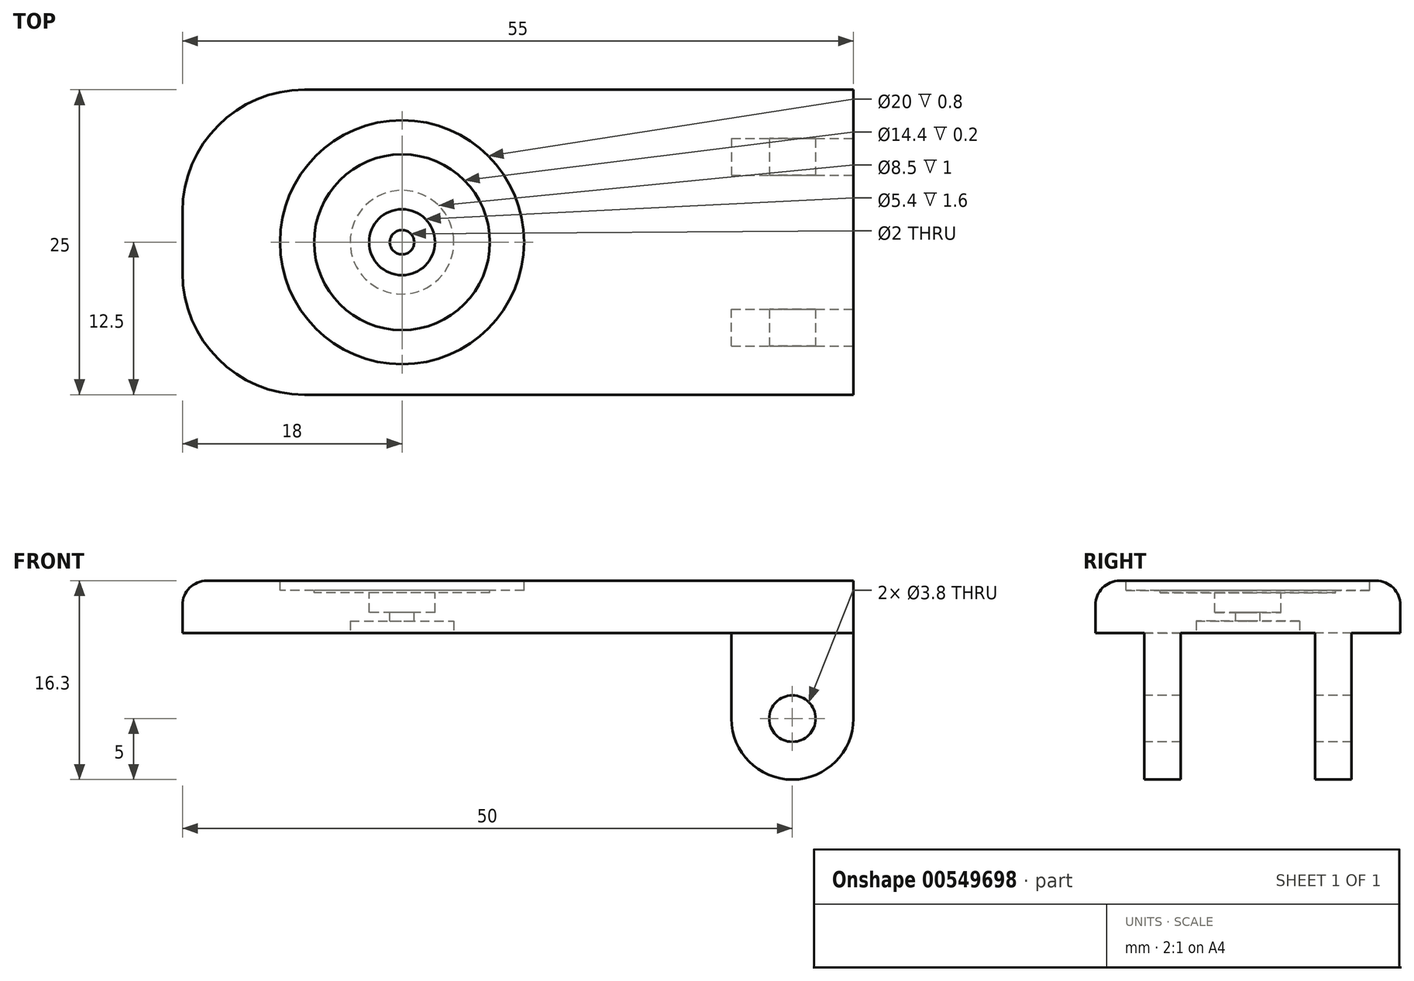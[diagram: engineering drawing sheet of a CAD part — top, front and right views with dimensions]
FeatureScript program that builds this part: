
annotation { "Feature Type Name" : "Feature", "Feature Type Description" : "" }
export const myFeature = defineFeature(function(context is Context, id is Id, definition is map)
    precondition{}
    {
        {
            var Q0;
            Q0=qCreatedBy(makeId("Top.planeOp"),FACE);
            var sketch = newSketch(context, id + "F0", { "sketchPlane" : qUnion([Q0])});
            skLineSegment(sketch, "E0.bottom", {"start": v(-45, 12.5) * mm, "end": v(0, 12.5) * mm});
            skLineSegment(sketch, "E0.top", {"start": v(-45, -12.5) * mm, "end": v(0, -12.5) * mm});
            skLineSegment(sketch, "E0.left", {"start": v(-55, 2.5) * mm, "end": v(-55, -2.5) * mm});
            skLineSegment(sketch, "E0.right", {"start": v(0, 12.5) * mm, "end": v(0, -12.5) * mm});
            skCircle(sketch, "E1", {"center": v(-37, 0) * mm, "radius": 10 * mm});
            skLineSegment(sketch, "E2", {"start": v(-55, 0) * mm, "end": v(0, 0) * mm, "construction": true});
            skPoint(sketch, "E3.visualSharp", {"position": v(-55, 12.5) * mm});
            skArc(sketch, "E3.filletArc", {"start": v(-45, 12.5) * mm, "mid": v(-52.07, 9.57) * mm, "end": v(-55, 2.5) * mm});
            skPoint(sketch, "E4.visualSharp", {"position": v(-55, -12.5) * mm});
            skArc(sketch, "E4.filletArc", {"start": v(-55, -2.5) * mm, "mid": v(-52.07, -9.57) * mm, "end": v(-45, -12.5) * mm});
            skCircle(sketch, "E5", {"center": v(-37, 0) * mm, "radius": 7.2 * mm});
            skCircle(sketch, "E6", {"center": v(-37, 0) * mm, "radius": 2.7 * mm});
            skSolve(sketch);
        }
        {
            var Q0;
            Q0 = qSketchRegion(id + "F0", true);
            var Q1;
            Q1=makeQuery(id+"F0.imprint","IMPRINT",FACE,{"disambiguationData":[TD([[makeQuery(id+"F0.imprint","IMPRINT",EDGE,{"derivedFrom":sQuery(id+"F0.wireOp",EDGE,"E1")}),1.0]])]});
            var Q2;
            Q2=makeQuery(id+"F0.imprint","IMPRINT",FACE,{"disambiguationData":[TD([[makeQuery(id+"F0.imprint","IMPRINT",EDGE,{"derivedFrom":sQuery(id+"F0.wireOp",EDGE,"E5")}),1.0]])]});
            var Q3;
            Q3=makeQuery(id+"F0.imprint","IMPRINT",FACE,{"disambiguationData":[TD([[makeQuery(id+"F0.imprint","IMPRINT",EDGE,{"derivedFrom":sQuery(id+"F0.wireOp",EDGE,"E6")}),1.0]])]});
            extrude(context, id + "F1", {"entities" : qUnion([Q0, Q1, Q2, Q3]), "oppositeDirection" : true, "depth" : 4.3 * mm, "offsetDistance" : 25 * mm});
        }
        {
            var Q0;
            Q0=makeQuery(id+"F0.imprint","IMPRINT",FACE,{"disambiguationData":[TD([[makeQuery(id+"F0.imprint","IMPRINT",EDGE,{"derivedFrom":sQuery(id+"F0.wireOp",EDGE,"E1")}),1.0]])]});
            var Q1;
            Q1=makeQuery(id+"F0.imprint","IMPRINT",FACE,{"disambiguationData":[TD([[makeQuery(id+"F0.imprint","IMPRINT",EDGE,{"derivedFrom":sQuery(id+"F0.wireOp",EDGE,"E5")}),1.0]])]});
            extrude(context, id + "F2", {"entities" : qUnion([Q0, Q1]), "operationType" : NewBodyOperationType.REMOVE, "oppositeDirection" : true, "depth" : .8 * mm, "offsetDistance" : 25 * mm});
        }
        {
            var Q0;
            Q0=makeQuery(id+"F0.imprint","IMPRINT",FACE,{"disambiguationData":[TD([[makeQuery(id+"F0.imprint","IMPRINT",EDGE,{"derivedFrom":sQuery(id+"F0.wireOp",EDGE,"E5")}),1.0]])]});
            extrude(context, id + "F3", {"entities" : qUnion([Q0]), "operationType" : NewBodyOperationType.REMOVE, "oppositeDirection" : true, "depth" : 1 * mm, "offsetDistance" : 25 * mm});
        }
        {
            var Q0;
            Q0=makeQuery(id+"F1.opExtrude","CAP_FACE",FACE,{"disambiguationData":[OSD([sQuery(id+"F0.wireOp",EDGE,"E0.bottom"),sQuery(id+"F0.wireOp",EDGE,"E0.top"),sQuery(id+"F0.wireOp",EDGE,"E0.left"),sQuery(id+"F0.wireOp",EDGE,"E0.right"),sQuery(id+"F0.wireOp",EDGE,"E3.filletArc"),sQuery(id+"F0.wireOp",EDGE,"E4.filletArc"),sQuery(id+"F0.wireOp",EDGE,"E6")])],"isStart":false});
            var sketch = newSketch(context, id + "F4", { "sketchPlane" : qUnion([Q0])});
            skCircle(sketch, "E7", {"center": v(-37, 0) * mm, "radius": 4.25 * mm});
            skLineSegment(sketch, "E8.bottom", {"start": v(-10, 8.5) * mm, "end": v(0, 8.5) * mm});
            skLineSegment(sketch, "E8.top", {"start": v(-10, 5.5) * mm, "end": v(0, 5.5) * mm});
            skLineSegment(sketch, "E8.left", {"start": v(-10, 8.5) * mm, "end": v(-10, 5.5) * mm});
            skLineSegment(sketch, "E8.right", {"start": v(0, 8.5) * mm, "end": v(0, 5.5) * mm});
            skLineSegment(sketch, "E9.MirrorCS", {"start": v(-10, -8.5) * mm, "end": v(0, -8.5) * mm});
            skLineSegment(sketch, "E10.MirrorCS", {"start": v(0, -8.5) * mm, "end": v(0, -5.5) * mm});
            skLineSegment(sketch, "E11.MirrorCS", {"start": v(-10, -5.5) * mm, "end": v(0, -5.5) * mm});
            skLineSegment(sketch, "E12.MirrorCS", {"start": v(-10, -8.5) * mm, "end": v(-10, -5.5) * mm});
            skSolve(sketch);
        }
        {
            var Q0;
            Q0=makeQuery(id+"F4.imprint","IMPRINT",FACE,{"disambiguationData":[TD([[makeQuery(id+"F4.imprint","IMPRINT",EDGE,{"derivedFrom":sQuery(id+"F4.wireOp",EDGE,"E7")}),1.0]])]});
            extrude(context, id + "F5", {"entities" : qUnion([Q0]), "operationType" : NewBodyOperationType.REMOVE, "oppositeDirection" : true, "depth" : 1 * mm, "offsetDistance" : 25 * mm});
        }
        {
            var Q0;
            Q0=makeQuery(id+"F4.imprint","IMPRINT",FACE,{"disambiguationData":[TD([[makeQuery(id+"F4.imprint","IMPRINT",EDGE,{"derivedFrom":sQuery(id+"F4.wireOp",EDGE,"E8.bottom")}),-1.0]])]});
            var Q1;
            Q1=makeQuery(id+"F4.imprint","IMPRINT",FACE,{"disambiguationData":[TD([[makeQuery(id+"F4.imprint","IMPRINT",EDGE,{"derivedFrom":sQuery(id+"F4.wireOp",EDGE,"E9.MirrorCS")}),1.0]])]});
            extrude(context, id + "F6", {"entities" : qUnion([Q0, Q1]), "operationType" : NewBodyOperationType.ADD, "depth" : 12 * mm, "offsetDistance" : 25 * mm});
        }
        {
            var Q0;
            Q0=makeQuery(id+"F6.opExtrude","SWEPT_FACE",FACE,{"disambiguationData":[OSD([sQuery(id+"F4.wireOp",EDGE,"E8.bottom")])]});
            var sketch = newSketch(context, id + "F7", { "sketchPlane" : qUnion([Q0])});
            skLineSegment(sketch, "E13", {"start": v(-5, -16.3) * mm, "end": v(-5, -4.3) * mm, "construction": true});
            skCircle(sketch, "E14", {"center": v(-5, -11.3) * mm, "radius": 1.9 * mm});
            skSolve(sketch);
        }
        {
            var Q0;
            Q0=makeQuery(id+"F6.opExtrude","CAP_EDGE",EDGE,{"disambiguationData":[OSD([sQuery(id+"F4.wireOp",EDGE,"E8.right")])],"isStart":false});
            var Q1;
            Q1=makeQuery(id+"F6.opExtrude","CAP_EDGE",EDGE,{"disambiguationData":[OSD([sQuery(id+"F4.wireOp",EDGE,"E10.MirrorCS")])],"isStart":false});
            var Q2;
            Q2=makeQuery(id+"F6.opExtrude","CAP_EDGE",EDGE,{"disambiguationData":[OSD([sQuery(id+"F4.wireOp",EDGE,"E12.MirrorCS")])],"isStart":false});
            var Q3;
            Q3=makeQuery(id+"F6.opExtrude","CAP_EDGE",EDGE,{"disambiguationData":[OSD([sQuery(id+"F4.wireOp",EDGE,"E8.left")])],"isStart":false});
            fillet(context, id + "F8", {"entities" : qUnion([Q0, Q1, Q2, Q3]), "radius" : 5 * mm, "tangentPropagation" : true, "allowEdgeOverflow" : false});
        }
        {
            var Q0;
            Q0=makeQuery(id+"F7.imprint","IMPRINT",FACE,{"disambiguationData":[TD([[makeQuery(id+"F7.imprint","IMPRINT",EDGE,{"derivedFrom":sQuery(id+"F7.wireOp",EDGE,"E14")}),1.0]])]});
            var Q1;
            Q1=sQuery(id+"F7.wireOp",EDGE,"E14");
            extrude(context, id + "F9", {"entities" : qUnion([Q0]), "operationType" : NewBodyOperationType.REMOVE, "surfaceEntities" : qUnion([Q1]), "oppositeDirection" : true, "depth" : 25 * mm, "offsetDistance" : 25 * mm});
        }
        {
            var Q0;
            Q0=makeQuery(id+"F1.opExtrude","CAP_EDGE",EDGE,{"disambiguationData":[OSD([sQuery(id+"F0.wireOp",EDGE,"E0.top")])],"isStart":true});
            fillet(context, id + "F10", {"entities" : qUnion([Q0]), "radius" : 2 * mm, "tangentPropagation" : true, "allowEdgeOverflow" : false});
        }
        {
            var Q0;
            Q0=makeQuery(id+"F2.boolean.opBoolean","SPLIT",FACE,{"disambiguationData":[TD([makeQuery(id+"F2.opExtrude","SWEPT_FACE",FACE,{"disambiguationData":[OSD([sQuery(id+"F0.wireOp",EDGE,"E6")])]})])],"derivedFrom":makeQuery(id+"F1.opExtrude","CAP_FACE",FACE,{"disambiguationData":[OSD([sQuery(id+"F0.wireOp",EDGE,"E0.bottom"),sQuery(id+"F0.wireOp",EDGE,"E0.top"),sQuery(id+"F0.wireOp",EDGE,"E0.left"),sQuery(id+"F0.wireOp",EDGE,"E0.right"),sQuery(id+"F0.wireOp",EDGE,"E3.filletArc"),sQuery(id+"F0.wireOp",EDGE,"E4.filletArc")])],"isStart":true})});
            extrude(context, id + "F11", {"entities" : qUnion([Q0]), "operationType" : NewBodyOperationType.REMOVE, "oppositeDirection" : true, "depth" : 2.6 * mm, "offsetDistance" : 25 * mm});
        }
        {
            var Q0;
            Q0=sQuery(id+"F0.wireOp",VERTEX,"E1.center");
            var Q1;
            Q1=makeQuery(id+"F1.opExtrude","SWEPT_BODY",BODY,{"disambiguationData":[OSD([sQuery(id+"F0.wireOp",EDGE,"E0.bottom"),sQuery(id+"F0.wireOp",EDGE,"E0.top"),sQuery(id+"F0.wireOp",EDGE,"E0.left"),sQuery(id+"F0.wireOp",EDGE,"E0.right"),sQuery(id+"F0.wireOp",EDGE,"E3.filletArc"),sQuery(id+"F0.wireOp",EDGE,"E4.filletArc")])]});
            hole(context, id + "F12", {"style" : HoleStyle.SIMPLE, "endStyle" : HoleEndStyle.THROUGH, "holeDiameter" : 2 * mm, "isTappedThrough" : true, "tappedDepth" : 12 * mm, "tapClearance" : 3, "locations" : qUnion([Q0]), "scope" : qUnion([Q1])});
        }
    });
